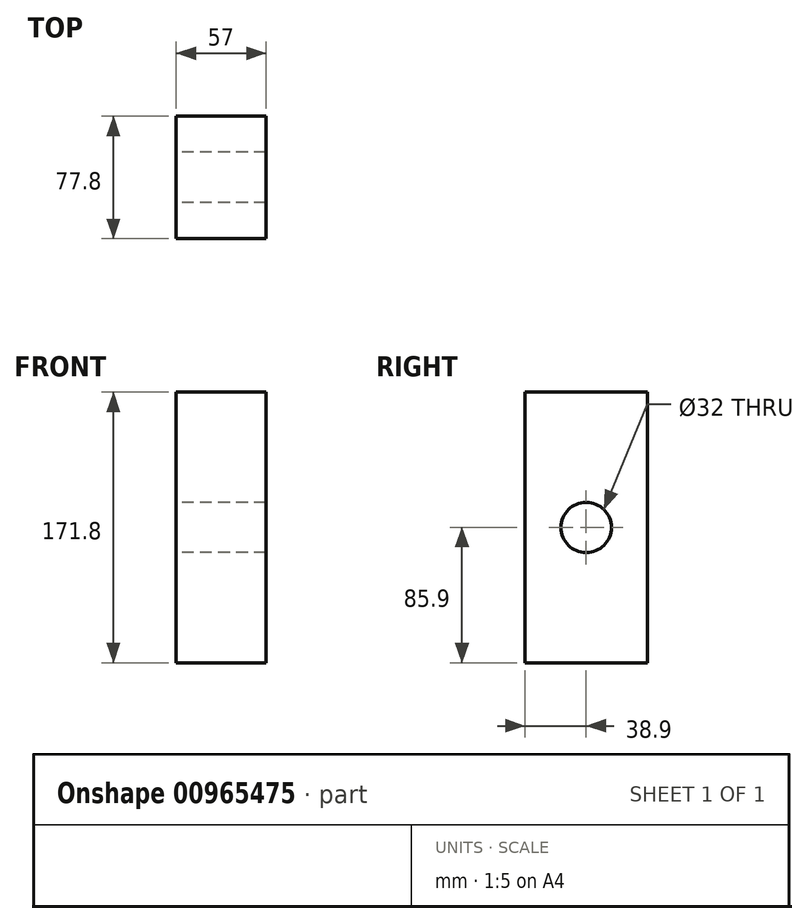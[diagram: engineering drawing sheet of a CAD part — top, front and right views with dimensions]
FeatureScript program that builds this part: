
annotation { "Feature Type Name" : "Feature", "Feature Type Description" : "" }
export const myFeature = defineFeature(function(context is Context, id is Id, definition is map)
    precondition{}
    {
        {
            var Q0;
            Q0=qCreatedBy(makeId("Right.planeOp"),FACE);
            var sketch = newSketch(context, id + "F0", { "sketchPlane" : qUnion([Q0])});
            skLineSegment(sketch, "E0.0", {"start": v(-38.9, 85.9) * mm, "end": v(38.9, 85.9) * mm});
            skLineSegment(sketch, "E0.1", {"start": v(-38.9, 85.9) * mm, "end": v(-38.9, -85.9) * mm});
            skLineSegment(sketch, "E0.2", {"start": v(-38.9, -85.9) * mm, "end": v(38.9, -85.9) * mm});
            skLineSegment(sketch, "E0.3", {"start": v(38.9, 85.9) * mm, "end": v(38.9, -85.9) * mm});
            skCircle(sketch, "E1", {"center": v(0, 0) * mm, "radius": 16 * mm});
            skSolve(sketch);
        }
        {
            var Q0;
            Q0 = qSketchRegion(id + "F0", true);
            extrude(context, id + "F1", {"entities" : qUnion([Q0]), "depth" : 57 * mm, "offsetDistance" : 25.4 * mm});
        }
    });
